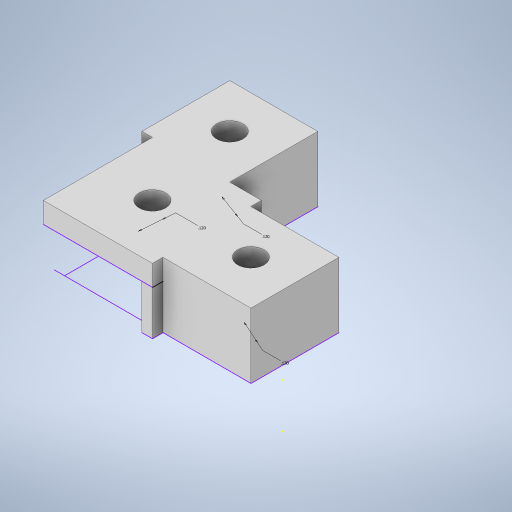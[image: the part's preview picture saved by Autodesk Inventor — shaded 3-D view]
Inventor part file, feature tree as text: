
AUTODESK INVENTOR PART (.ipt)
format: ipt  version: 2024 (Build 280153000, 153)  size: 267,776 bytes
history: native  units: in
note: dims shown in document units (in); Inventor stores cm internally (conversion verified against a paired STEP export)
features: extrude x4, hole x3, sketch x2
ambient origin geometry x8: Origin, YZ Plane, XZ Plane, XY Plane, X Axis, Y Axis, Z Axis, Center Point
bodies: Solid1 (feature_tree)
feature tree (9):
  sketch  "Sketch1"  dims[d0=0.202in d1=0.0in d2=0.094in d3=0.0in]
  extrude  "Extrusion1"  Depth=0.094in TaperAngle=0.0deg
  sketch  "Sketch2"  dims[d4=0.12in d5=0.12in d6=0.75in d7=0.375in d8=0.25in d9=0.5635in d10=1.0in d11=0.8108in d12=0.296in d13=0.0in d14=0.296in d15=0.0in d16=0.12in d17=0.12in d18=0.12in d19=0.75in d20=0.375in d21=0.25in d22=0.5635in d23=1.0in d24=0.8108in d25=0.12in d26=0.75in d27=0.375in d28=0.25in d29=0.5635in d30=1.0in d31=0.8108in]
  extrude  "Extrusion2"  Depth=0.296in TaperAngle=0.0deg
  hole  "Hole1"  [1 undecoded]
  extrude  "Extrusion3"  Depth=0.296in
  extrude  "Extrusion4"  Depth=0.296in
  hole  "Hole2"  [1 undecoded]
  hole  "Hole3"  [1 undecoded]
note: 3 required parameter values undecoded (feature->parameter linkage not recoverable at this tier; creation-order binding heuristic only, values carry confidence <= 0.55)
